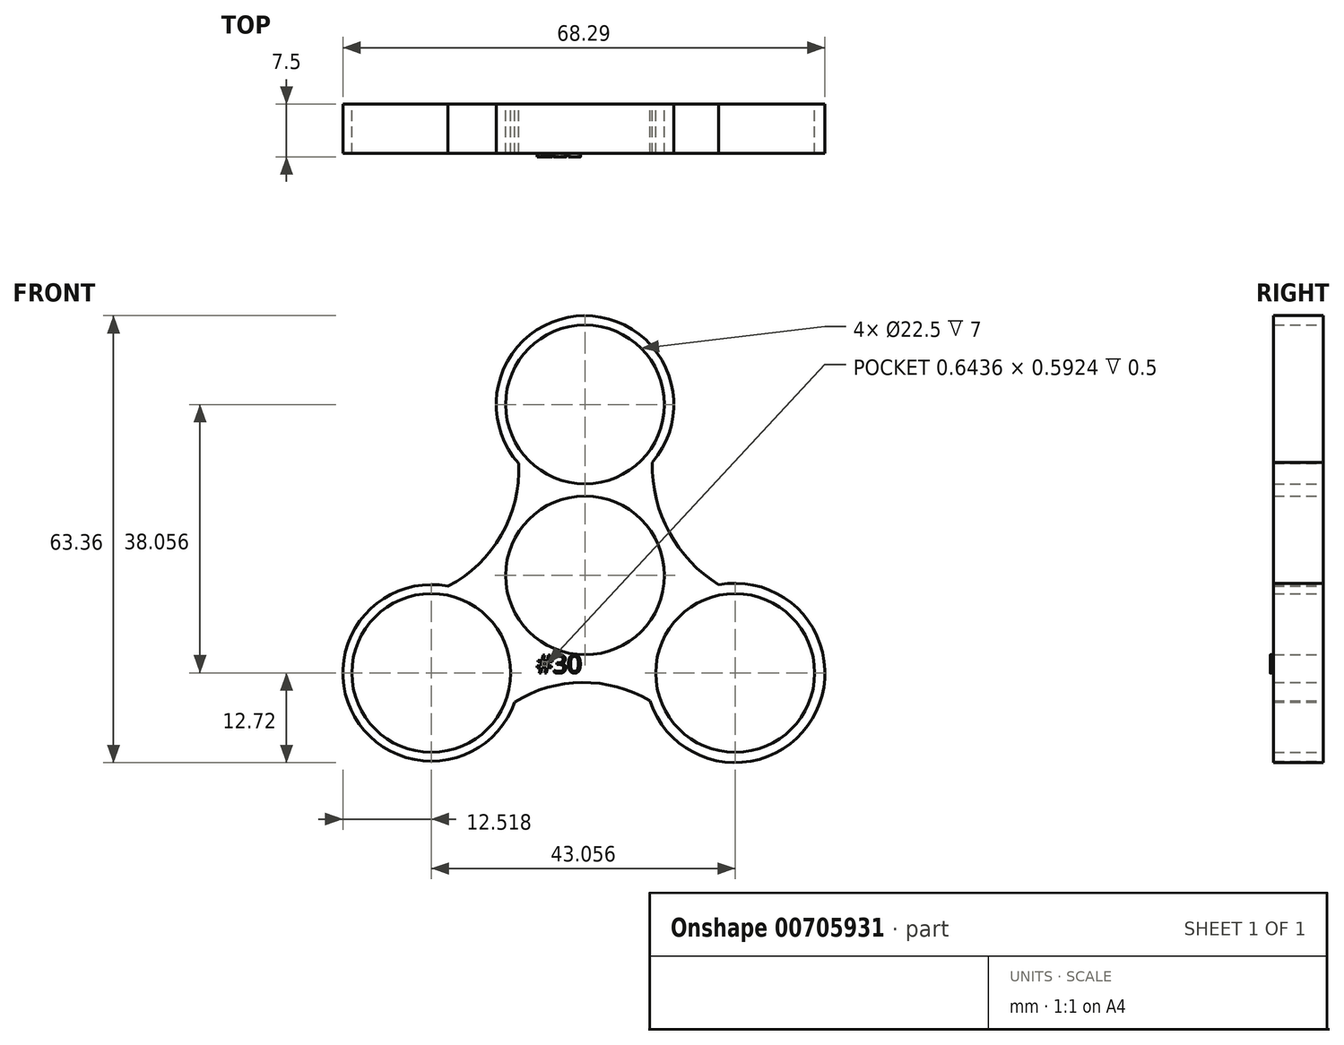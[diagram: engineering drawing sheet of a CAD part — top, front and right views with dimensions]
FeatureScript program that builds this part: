
annotation { "Feature Type Name" : "Feature", "Feature Type Description" : "" }
export const myFeature = defineFeature(function(context is Context, id is Id, definition is map)
    precondition{}
    {
        {
            var Q0;
            Q0=qCreatedBy(makeId("Front.planeOp"),FACE);
            var sketch = newSketch(context, id + "F0", { "sketchPlane" : qUnion([Q0])});
            skCircle(sketch, "E0", {"center": v(0, 13.82) * mm, "radius": 11.25 * mm});
            skCircle(sketch, "E1", {"center": v(0, 38.06) * mm, "radius": 11.25 * mm});
            skCircle(sketch, "E2", {"center": v(21.27, 0) * mm, "radius": 11.25 * mm});
            skCircle(sketch, "E3", {"center": v(-21.78, 0) * mm, "radius": 11.25 * mm});
            skLineSegment(sketch, "E4", {"start": v(0, 38.06) * mm, "end": v(0, 52.64) * mm});
            skLineSegment(sketch, "E5", {"start": v(0, 38.06) * mm, "end": v(-13.8, 30.08) * mm});
            skLineSegment(sketch, "E6", {"start": v(-21.78, 0) * mm, "end": v(-21.78, 13.93) * mm});
            skLineSegment(sketch, "E7", {"start": v(-21.78, 0) * mm, "end": v(-35.67, -8.02) * mm});
            skLineSegment(sketch, "E8", {"start": v(-21.78, 0) * mm, "end": v(-6.15, -9.02) * mm});
            skLineSegment(sketch, "E9", {"start": v(21.27, 0) * mm, "end": v(8.63, -7.3) * mm});
            skLineSegment(sketch, "E10", {"start": v(21.27, 0) * mm, "end": v(21.27, 13.93) * mm});
            skLineSegment(sketch, "E11", {"start": v(0, 38.06) * mm, "end": v(19, 27.08) * mm});
            skLineSegment(sketch, "E12", {"start": v(21.27, 0) * mm, "end": v(35.04, -7.95) * mm});
            skArc(sketch, "E13", {"start": v(9.74, 32.43) * mm, "mid": v(11.95, 19.9) * mm, "end": v(21.27, 11.25) * mm});
            skArc(sketch, "E14", {"start": v(-21.78, 11.25) * mm, "mid": v(-11.82, 19.6) * mm, "end": v(-9.74, 32.43) * mm});
            skArc(sketch, "E15", {"start": v(11.53, -5.62) * mm, "mid": v(-0.25, -1.35) * mm, "end": v(-12.04, -5.62) * mm});
            skCircle(sketch, "E16", {"center": v(-21.78, 0) * mm, "radius": 12.52 * mm});
            skCircle(sketch, "E17", {"center": v(0, 38.06) * mm, "radius": 12.58 * mm});
            skCircle(sketch, "E18", {"center": v(21.27, 0) * mm, "radius": 12.72 * mm});
            skSolve(sketch);
        }
        {
            var Q0;
            {var subQ1=sQuery(id+"F0.wireOp",EDGE,"E5");var subQ3=sQuery(id+"F0.wireOp",EDGE,"E17");var subQ4=makeQuery(id+"F0.imprint","INTERSECT",VERTEX,{"derivedFrom":[subQ1,subQ3]});Q0=makeQuery(id+"F0.imprint","IMPRINT",FACE,{"disambiguationData":[TD([[makeQuery(id+"F0.imprint","IMPRINT",EDGE,{"disambiguationData":[TD([[subQ4,-1.0]])],"derivedFrom":subQ3}),1.0]])]});}
            var Q1;
            {var subQ1=sQuery(id+"F0.wireOp",EDGE,"E6");var subQ3=sQuery(id+"F0.wireOp",EDGE,"E16");var subQ4=makeQuery(id+"F0.imprint","INTERSECT",VERTEX,{"derivedFrom":[subQ1,subQ3]});Q1=makeQuery(id+"F0.imprint","IMPRINT",FACE,{"disambiguationData":[TD([[makeQuery(id+"F0.imprint","IMPRINT",EDGE,{"disambiguationData":[TD([[subQ4,1.0]])],"derivedFrom":subQ3}),1.0]])]});}
            var Q2;
            {var subQ1=sQuery(id+"F0.wireOp",EDGE,"E8");var subQ3=sQuery(id+"F0.wireOp",EDGE,"E16");var subQ4=makeQuery(id+"F0.imprint","INTERSECT",VERTEX,{"derivedFrom":[subQ1,subQ3]});Q2=makeQuery(id+"F0.imprint","IMPRINT",FACE,{"disambiguationData":[TD([[makeQuery(id+"F0.imprint","IMPRINT",EDGE,{"disambiguationData":[TD([[subQ4,-1.0]])],"derivedFrom":subQ3}),1.0]])]});}
            var Q3;
            {var subQ1=sQuery(id+"F0.wireOp",EDGE,"E9");var subQ3=sQuery(id+"F0.wireOp",EDGE,"E18");var subQ4=makeQuery(id+"F0.imprint","INTERSECT",VERTEX,{"derivedFrom":[subQ1,subQ3]});Q3=makeQuery(id+"F0.imprint","IMPRINT",FACE,{"disambiguationData":[TD([[makeQuery(id+"F0.imprint","IMPRINT",EDGE,{"disambiguationData":[TD([[subQ4,1.0]])],"derivedFrom":subQ3}),1.0]])]});}
            var Q4;
            {var subQ1=sQuery(id+"F0.wireOp",EDGE,"E10");var subQ3=sQuery(id+"F0.wireOp",EDGE,"E18");var subQ4=makeQuery(id+"F0.imprint","INTERSECT",VERTEX,{"derivedFrom":[subQ1,subQ3]});Q4=makeQuery(id+"F0.imprint","IMPRINT",FACE,{"disambiguationData":[TD([[makeQuery(id+"F0.imprint","IMPRINT",EDGE,{"disambiguationData":[TD([[subQ4,-1.0]])],"derivedFrom":subQ3}),1.0]])]});}
            var Q5;
            {var subQ1=sQuery(id+"F0.wireOp",EDGE,"E11");var subQ3=sQuery(id+"F0.wireOp",EDGE,"E17");var subQ4=makeQuery(id+"F0.imprint","INTERSECT",VERTEX,{"derivedFrom":[subQ1,subQ3]});Q5=makeQuery(id+"F0.imprint","IMPRINT",FACE,{"disambiguationData":[TD([[makeQuery(id+"F0.imprint","IMPRINT",EDGE,{"disambiguationData":[TD([[subQ4,1.0]])],"derivedFrom":subQ3}),1.0]])]});}
            var Q6;
            {var subQ3=sQuery(id+"F0.wireOp",EDGE,"E4");var subQ5=sQuery(id+"F0.wireOp",EDGE,"E17");var subQ6=makeQuery(id+"F0.imprint","INTERSECT",VERTEX,{"derivedFrom":[subQ3,subQ5]});Q6=makeQuery(id+"F0.imprint","IMPRINT",FACE,{"disambiguationData":[TD([[makeQuery(id+"F0.imprint","IMPRINT",EDGE,{"disambiguationData":[TD([[subQ6,1.0]])],"derivedFrom":subQ3}),1.0]])]});}
            var Q7;
            {var subQ3=sQuery(id+"F0.wireOp",EDGE,"E4");var subQ5=sQuery(id+"F0.wireOp",EDGE,"E17");var subQ6=makeQuery(id+"F0.imprint","INTERSECT",VERTEX,{"derivedFrom":[subQ3,subQ5]});Q7=makeQuery(id+"F0.imprint","IMPRINT",FACE,{"disambiguationData":[TD([[makeQuery(id+"F0.imprint","IMPRINT",EDGE,{"disambiguationData":[TD([[subQ6,1.0]])],"derivedFrom":subQ3}),-1.0]])]});}
            var Q8;
            {var subQ3=sQuery(id+"F0.wireOp",EDGE,"E12");var subQ5=sQuery(id+"F0.wireOp",EDGE,"E18");var subQ7=makeQuery(id+"F0.imprint","INTERSECT",VERTEX,{"derivedFrom":[subQ3,subQ5]});Q8=makeQuery(id+"F0.imprint","IMPRINT",FACE,{"disambiguationData":[TD([[makeQuery(id+"F0.imprint","IMPRINT",EDGE,{"disambiguationData":[TD([[subQ7,1.0]])],"derivedFrom":subQ3}),-1.0]])]});}
            var Q9;
            {var subQ3=sQuery(id+"F0.wireOp",EDGE,"E12");var subQ5=sQuery(id+"F0.wireOp",EDGE,"E18");var subQ7=makeQuery(id+"F0.imprint","INTERSECT",VERTEX,{"derivedFrom":[subQ3,subQ5]});Q9=makeQuery(id+"F0.imprint","IMPRINT",FACE,{"disambiguationData":[TD([[makeQuery(id+"F0.imprint","IMPRINT",EDGE,{"disambiguationData":[TD([[subQ7,1.0]])],"derivedFrom":subQ3}),1.0]])]});}
            var Q10;
            {var subQ3=sQuery(id+"F0.wireOp",EDGE,"E7");var subQ5=sQuery(id+"F0.wireOp",EDGE,"E16");var subQ6=makeQuery(id+"F0.imprint","INTERSECT",VERTEX,{"derivedFrom":[subQ3,subQ5]});Q10=makeQuery(id+"F0.imprint","IMPRINT",FACE,{"disambiguationData":[TD([[makeQuery(id+"F0.imprint","IMPRINT",EDGE,{"disambiguationData":[TD([[subQ6,1.0]])],"derivedFrom":subQ3}),-1.0]])]});}
            var Q11;
            {var subQ3=sQuery(id+"F0.wireOp",EDGE,"E7");var subQ5=sQuery(id+"F0.wireOp",EDGE,"E16");var subQ6=makeQuery(id+"F0.imprint","INTERSECT",VERTEX,{"derivedFrom":[subQ3,subQ5]});Q11=makeQuery(id+"F0.imprint","IMPRINT",FACE,{"disambiguationData":[TD([[makeQuery(id+"F0.imprint","IMPRINT",EDGE,{"disambiguationData":[TD([[subQ6,1.0]])],"derivedFrom":subQ3}),1.0]])]});}
            var Q12;
            {var subQ0=sQuery(id+"F0.wireOp",EDGE,"E13");var subQ5=sQuery(id+"F0.wireOp",EDGE,"E17");var subQ6=makeQuery(id+"F0.imprint","INTERSECT",VERTEX,{"derivedFrom":[subQ0,subQ5]});Q12=makeQuery(id+"F0.imprint","IMPRINT",FACE,{"disambiguationData":[TD([[makeQuery(id+"F0.imprint","IMPRINT",EDGE,{"disambiguationData":[TD([[subQ6,1.0]])],"derivedFrom":subQ5}),1.0]])]});}
            var Q13;
            {var subQ0=sQuery(id+"F0.wireOp",EDGE,"E13");var subQ5=sQuery(id+"F0.wireOp",EDGE,"E18");var subQ7=makeQuery(id+"F0.imprint","INTERSECT",VERTEX,{"derivedFrom":[subQ0,subQ5]});Q13=makeQuery(id+"F0.imprint","IMPRINT",FACE,{"disambiguationData":[TD([[makeQuery(id+"F0.imprint","IMPRINT",EDGE,{"disambiguationData":[TD([[subQ7,-1.0]])],"derivedFrom":subQ5}),1.0]])]});}
            var Q14;
            {var subQ0=sQuery(id+"F0.wireOp",EDGE,"E14");var subQ5=sQuery(id+"F0.wireOp",EDGE,"E16");var subQ6=makeQuery(id+"F0.imprint","INTERSECT",VERTEX,{"derivedFrom":[subQ0,subQ5]});Q14=makeQuery(id+"F0.imprint","IMPRINT",FACE,{"disambiguationData":[TD([[makeQuery(id+"F0.imprint","IMPRINT",EDGE,{"disambiguationData":[TD([[subQ6,1.0]])],"derivedFrom":subQ5}),1.0]])]});}
            var Q15;
            Q15=makeQuery(id+"F0.imprint","IMPRINT",FACE,{"disambiguationData":[TD([[makeQuery(id+"F0.imprint","IMPRINT",EDGE,{"derivedFrom":sQuery(id+"F0.wireOp",EDGE,"E0")}),-1.0]])]});
            extrude(context, id + "F1", {"entities" : qUnion([Q0, Q1, Q2, Q3, Q4, Q5, Q6, Q7, Q8, Q9, Q10, Q11, Q12, Q13, Q14, Q15]), "depth" : 7 * mm, "offsetDistance" : 25 * mm});
        }
        {
            var Q0;
            Q0=makeQuery(id+"F1.opExtrude","CAP_FACE",FACE,{"disambiguationData":[OSD([sQuery(id+"F0.wireOp",EDGE,"E0"),sQuery(id+"F0.wireOp",EDGE,"E1"),sQuery(id+"F0.wireOp",EDGE,"E2"),sQuery(id+"F0.wireOp",EDGE,"E3"),sQuery(id+"F0.wireOp",EDGE,"E13"),sQuery(id+"F0.wireOp",EDGE,"E14"),sQuery(id+"F0.wireOp",EDGE,"E15"),sQuery(id+"F0.wireOp",EDGE,"E16"),sQuery(id+"F0.wireOp",EDGE,"E17"),sQuery(id+"F0.wireOp",EDGE,"E18")])],"isStart":false});
            var sketch = newSketch(context, id + "F2", { "sketchPlane" : qUnion([Q0])});
            skText(sketch, "E19", { "text": "#30", "fontName": "OpenSans-Regular.ttf"});
            skPoint(sketch, "E19.secondSnap0", {"position": v(-0.4, -1.35) * mm});
            const initialGuessF2  = {"E19": [-0.00686, 0, 1, 0, 0.00257]};
            skSetInitialGuess(sketch, initialGuessF2);
            skSolve(sketch);
        }
        {
            var Q0;
            Q0 = qSketchRegion(id + "F2", true);
            extrude(context, id + "F3", {"entities" : qUnion([Q0]), "operationType" : NewBodyOperationType.ADD, "depth" : .5 * mm, "offsetDistance" : 25 * mm});
        }
    });
